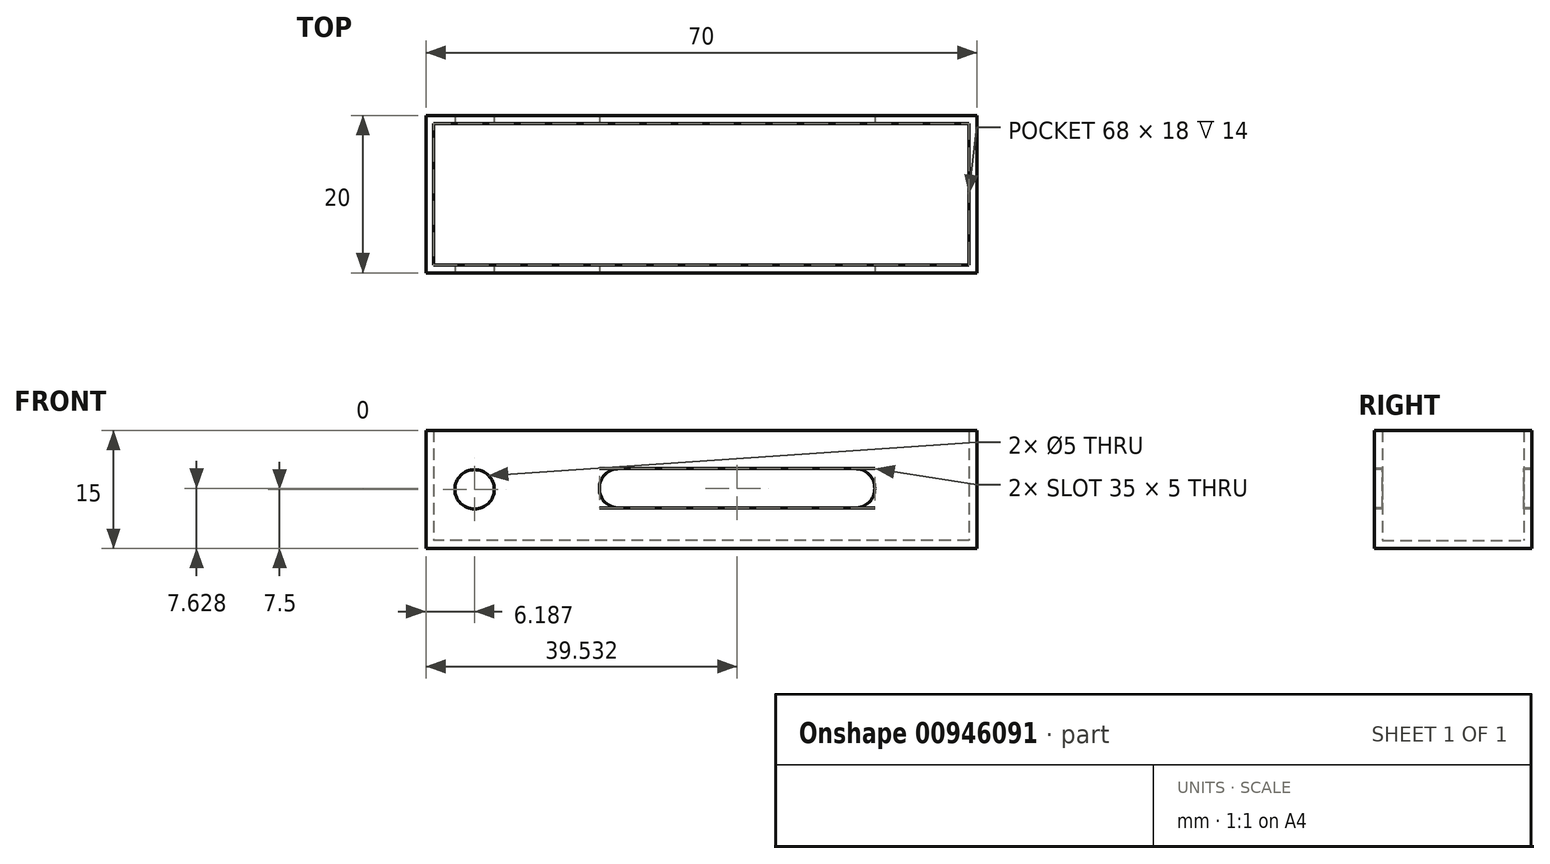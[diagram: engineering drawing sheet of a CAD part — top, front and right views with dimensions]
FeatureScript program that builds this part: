
annotation { "Feature Type Name" : "Feature", "Feature Type Description" : "" }
export const myFeature = defineFeature(function(context is Context, id is Id, definition is map)
    precondition{}
    {
        {
            var Q0;
            Q0=qCreatedBy(makeId("Top.planeOp"),FACE);
            var sketch = newSketch(context, id + "F0", { "sketchPlane" : qUnion([Q0])});
            skLineSegment(sketch, "E0.bottom", {"start": v(35, -8.41) * mm, "end": v(-35, -8.41) * mm});
            skLineSegment(sketch, "E0.top", {"start": v(35, 11.59) * mm, "end": v(-35, 11.59) * mm});
            skLineSegment(sketch, "E0.left", {"start": v(35, -8.41) * mm, "end": v(35, 11.59) * mm});
            skLineSegment(sketch, "E0.right", {"start": v(-35, -8.41) * mm, "end": v(-35, 11.59) * mm});
            skPoint(sketch, "E0.middle", {"position": v(0, 1.59) * mm});
            skSolve(sketch);
        }
        {
            var Q0;
            Q0=makeQuery(id+"F0.imprint","IMPRINT",FACE,{"disambiguationData":[TD([[makeQuery(id+"F0.imprint","IMPRINT",EDGE,{"derivedFrom":sQuery(id+"F0.wireOp",EDGE,"E0.bottom")}),-1.0]])]});
            extrude(context, id + "F1", {"entities" : qUnion([Q0]), "depth" : 15 * mm, "offsetDistance" : 25 * mm});
        }
        {
            var Q0;
            Q0=makeQuery(id+"F1.opExtrude","SWEPT_FACE",FACE,{"disambiguationData":[OSD([sQuery(id+"F0.wireOp",EDGE,"E0.bottom")])]});
            var sketch = newSketch(context, id + "F2", { "sketchPlane" : qUnion([Q0])});
            skCircle(sketch, "E1", {"center": v(-28.81, 7.5) * mm, "radius": 2.5 * mm});
            skPoint(sketch, "E2.middle", {"position": v(4.53, 7.63) * mm});
            skLineSegment(sketch, "E3.bottom", {"start": v(22.03, 5.13) * mm, "end": v(-12.97, 5.13) * mm});
            skLineSegment(sketch, "E3.top", {"start": v(22.03, 10.13) * mm, "end": v(-12.97, 10.13) * mm});
            skLineSegment(sketch, "E3.left", {"start": v(22.03, 5.13) * mm, "end": v(22.03, 10.13) * mm});
            skLineSegment(sketch, "E3.right", {"start": v(-12.97, 5.13) * mm, "end": v(-12.97, 10.13) * mm});
            skSolve(sketch);
        }
        {
            var Q0;
            Q0=makeQuery(id+"F1.opExtrude","CAP_FACE",FACE,{"disambiguationData":[OSD([sQuery(id+"F0.wireOp",EDGE,"E0.bottom"),sQuery(id+"F0.wireOp",EDGE,"E0.top"),sQuery(id+"F0.wireOp",EDGE,"E0.left"),sQuery(id+"F0.wireOp",EDGE,"E0.right")])],"isStart":false});
            shell(context, id + "F3", {"entities" : qUnion([Q0]), "thickness" : 1 * mm});
        }
        {
            var Q0;
            Q0=sQuery(id+"F2.wireOp",VERTEX,"E1.center");
            var Q1;
            Q1=makeQuery(id+"F1.opExtrude","SWEPT_BODY",BODY,{"disambiguationData":[OSD([sQuery(id+"F0.wireOp",EDGE,"E0.bottom"),sQuery(id+"F0.wireOp",EDGE,"E0.top"),sQuery(id+"F0.wireOp",EDGE,"E0.left"),sQuery(id+"F0.wireOp",EDGE,"E0.right")])]});
            hole(context, id + "F4", {"style" : HoleStyle.SIMPLE, "endStyle" : HoleEndStyle.THROUGH, "holeDiameter" : 5 * mm, "majorDiameter" : 5 * mm, "isTappedThrough" : true, "tappedDepth" : 12 * mm, "tapClearance" : 3, "locations" : qUnion([Q0]), "scope" : qUnion([Q1])});
        }
        {
            var Q0;
            Q0=makeQuery(id+"F2.imprint","IMPRINT",FACE,{"disambiguationData":[TD([[makeQuery(id+"F2.imprint","IMPRINT",EDGE,{"derivedFrom":sQuery(id+"F2.wireOp",EDGE,"E3.bottom")}),-1.0]])]});
            extrude(context, id + "F5", {"entities" : qUnion([Q0]), "operationType" : NewBodyOperationType.REMOVE, "oppositeDirection" : true, "depth" : 25 * mm, "offsetDistance" : 25 * mm});
        }
        {
            var Q0;
            {var subQ0=sQuery(id+"F0.wireOp",EDGE,"E0.bottom");var subQ1=sQuery(id+"F2.wireOp",EDGE,"E3.top");var subQ2=sQuery(id+"F2.wireOp",EDGE,"E3.right");Q0=makeQuery(id+"F5.boolean.opBoolean","COPY",EDGE,{"disambiguationData":[TD([makeQuery(id+"F1.opExtrude","SWEPT_FACE",FACE,{"disambiguationData":[OSD([subQ0])]})])],"derivedFrom":makeQuery(id+"F5.opExtrude","SWEPT_EDGE",EDGE,{"disambiguationData":[OSD([subQ1,subQ2])]})});}
            var Q1;
            {var subQ0=sQuery(id+"F0.wireOp",EDGE,"E0.bottom");var subQ1=sQuery(id+"F2.wireOp",EDGE,"E3.bottom");var subQ2=sQuery(id+"F2.wireOp",EDGE,"E3.right");Q1=makeQuery(id+"F5.boolean.opBoolean","COPY",EDGE,{"disambiguationData":[TD([makeQuery(id+"F1.opExtrude","SWEPT_FACE",FACE,{"disambiguationData":[OSD([subQ0])]})])],"derivedFrom":makeQuery(id+"F5.opExtrude","SWEPT_EDGE",EDGE,{"disambiguationData":[OSD([subQ1,subQ2])]})});}
            var Q2;
            {var subQ0=sQuery(id+"F0.wireOp",EDGE,"E0.bottom");var subQ1=sQuery(id+"F2.wireOp",EDGE,"E3.left");var subQ2=sQuery(id+"F2.wireOp",EDGE,"E3.bottom");Q2=makeQuery(id+"F5.boolean.opBoolean","COPY",EDGE,{"disambiguationData":[TD([makeQuery(id+"F1.opExtrude","SWEPT_FACE",FACE,{"disambiguationData":[OSD([subQ0])]})])],"derivedFrom":makeQuery(id+"F5.opExtrude","SWEPT_EDGE",EDGE,{"disambiguationData":[OSD([subQ2,subQ1])]})});}
            var Q3;
            {var subQ0=sQuery(id+"F0.wireOp",EDGE,"E0.bottom");var subQ1=sQuery(id+"F2.wireOp",EDGE,"E3.left");var subQ2=sQuery(id+"F2.wireOp",EDGE,"E3.top");Q3=makeQuery(id+"F5.boolean.opBoolean","COPY",EDGE,{"disambiguationData":[TD([makeQuery(id+"F1.opExtrude","SWEPT_FACE",FACE,{"disambiguationData":[OSD([subQ0])]})])],"derivedFrom":makeQuery(id+"F5.opExtrude","SWEPT_EDGE",EDGE,{"disambiguationData":[OSD([subQ2,subQ1])]})});}
            fillet(context, id + "F6", {"entities" : qUnion([Q0, Q1, Q2, Q3]), "radius" : 2.5 * mm, "tangentPropagation" : true, "allowEdgeOverflow" : false});
        }
    });
